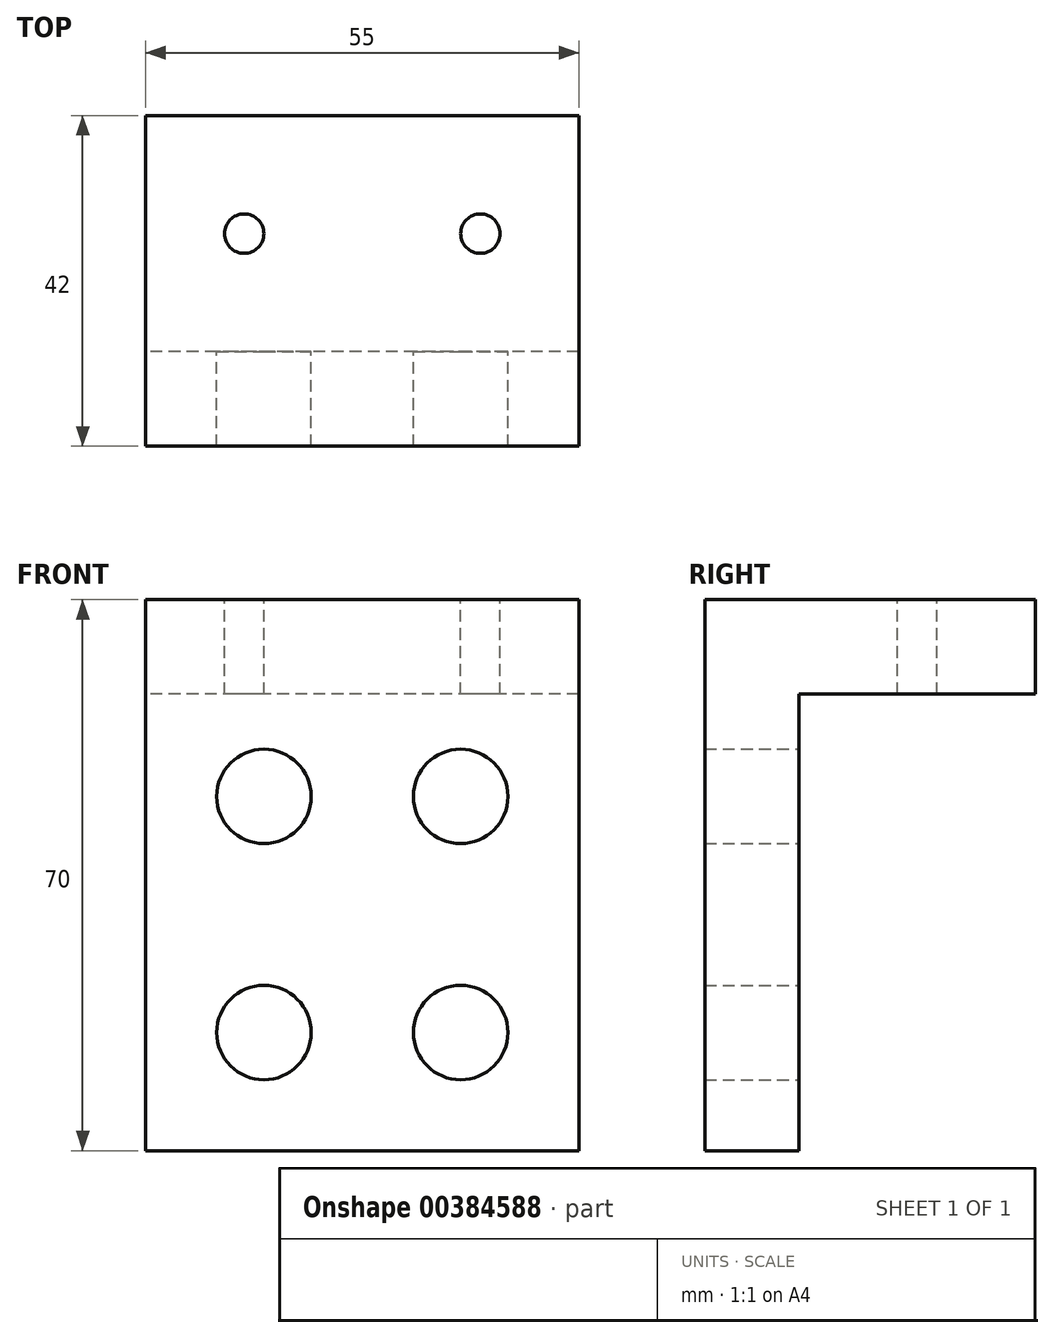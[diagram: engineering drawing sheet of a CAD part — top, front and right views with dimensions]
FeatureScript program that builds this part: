
annotation { "Feature Type Name" : "Feature", "Feature Type Description" : "" }
export const myFeature = defineFeature(function(context is Context, id is Id, definition is map)
    precondition{}
    {
        {
            var Q0;
            Q0=qCreatedBy(makeId("Top.planeOp"),FACE);
            var sketch = newSketch(context, id + "F0", { "sketchPlane" : qUnion([Q0])});
            skLineSegment(sketch, "E0.bottom", {"start": v(27.5, -15) * mm, "end": v(-27.5, -15) * mm});
            skLineSegment(sketch, "E0.top", {"start": v(27.5, 15) * mm, "end": v(-27.5, 15) * mm});
            skLineSegment(sketch, "E0.left", {"start": v(27.5, -15) * mm, "end": v(27.5, 15) * mm});
            skLineSegment(sketch, "E0.right", {"start": v(-27.5, -15) * mm, "end": v(-27.5, 15) * mm});
            skPoint(sketch, "E0.middle", {"position": v(0, 0) * mm});
            skSolve(sketch);
        }
        {
            var Q0;
            Q0=makeQuery(id+"F0.imprint","IMPRINT",FACE,{"disambiguationData":[TD([[makeQuery(id+"F0.imprint","IMPRINT",EDGE,{"derivedFrom":sQuery(id+"F0.wireOp",EDGE,"E0.bottom")}),-1.0]])]});
            extrude(context, id + "F1", {"entities" : qUnion([Q0]), "depth" : 12 * mm});
        }
        {
            var Q0;
            Q0=makeQuery(id+"F1.opExtrude","CAP_FACE",FACE,{"disambiguationData":[OSD([sQuery(id+"F0.wireOp",EDGE,"E0.bottom"),sQuery(id+"F0.wireOp",EDGE,"E0.top"),sQuery(id+"F0.wireOp",EDGE,"E0.left"),sQuery(id+"F0.wireOp",EDGE,"E0.right")])],"isStart":false});
            var sketch = newSketch(context, id + "F2", { "sketchPlane" : qUnion([Q0])});
            skLineSegment(sketch, "E1", {"start": v(-27.5, 0) * mm, "end": v(-15, 0) * mm, "construction": true});
            skLineSegment(sketch, "E2", {"start": v(-15, 0) * mm, "end": v(15, 0) * mm, "construction": true});
            skLineSegment(sketch, "E3", {"start": v(15, 0) * mm, "end": v(27.5, 0) * mm, "construction": true});
            skSolve(sketch);
        }
        {
            var Q0;
            Q0=sQuery(id+"F2.wireOp",VERTEX,"E2.start");
            var Q1;
            Q1=sQuery(id+"F2.wireOp",VERTEX,"E3.start");
            var Q2;
            Q2=makeQuery(id+"F1.opExtrude","SWEPT_BODY",BODY,{"disambiguationData":[OSD([sQuery(id+"F0.wireOp",EDGE,"E0.bottom"),sQuery(id+"F0.wireOp",EDGE,"E0.top"),sQuery(id+"F0.wireOp",EDGE,"E0.left"),sQuery(id+"F0.wireOp",EDGE,"E0.right")])]});
            hole(context, id + "F3", {"style" : HoleStyle.SIMPLE, "endStyle" : HoleEndStyle.BLIND, "holeDiameter" : 5 * mm, "holeDepth" : 25 * mm, "isTappedThrough" : true, "tappedDepth" : 12 * mm, "tapClearance" : 3, "locations" : qUnion([Q0, Q1]), "scope" : qUnion([Q2])});
        }
        {
            var Q0;
            Q0=makeQuery(id+"F1.opExtrude","SWEPT_FACE",FACE,{"disambiguationData":[OSD([sQuery(id+"F0.wireOp",EDGE,"E0.bottom")])]});
            var sketch = newSketch(context, id + "F4", { "sketchPlane" : qUnion([Q0])});
            skLineSegment(sketch, "E4.bottom", {"start": v(-27.5, 12) * mm, "end": v(27.5, 12) * mm});
            skLineSegment(sketch, "E4.top", {"start": v(-27.5, -58) * mm, "end": v(27.5, -58) * mm});
            skLineSegment(sketch, "E4.left", {"start": v(-27.5, 12) * mm, "end": v(-27.5, -58) * mm});
            skLineSegment(sketch, "E4.right", {"start": v(27.5, 12) * mm, "end": v(27.5, -58) * mm});
            skSolve(sketch);
        }
        {
            var Q0;
            {var subQ0=sQuery(id+"F4.wireOp",EDGE,"E4.top");Q0=makeQuery(id+"F4.imprint","IMPRINT",FACE,{"disambiguationData":[TD([[makeQuery(id+"F4.imprint","IMPRINT",EDGE,{"derivedFrom":subQ0}),1.0]])]});}
            var Q1;
            {var subQ0=sQuery(id+"F4.wireOp",EDGE,"E4.bottom");Q1=makeQuery(id+"F4.imprint","IMPRINT",FACE,{"disambiguationData":[TD([[makeQuery(id+"F4.imprint","IMPRINT",EDGE,{"derivedFrom":subQ0}),1.0]])]});}
            extrude(context, id + "F5", {"entities" : qUnion([Q0, Q1]), "operationType" : NewBodyOperationType.ADD, "depth" : 12 * mm});
        }
        {
            var Q0;
            Q0=makeQuery(id+"F5.opExtrude","CAP_FACE",FACE,{"disambiguationData":[OSD([sQuery(id+"F4.wireOp",EDGE,"E4.bottom"),sQuery(id+"F4.wireOp",EDGE,"E4.top"),sQuery(id+"F4.wireOp",EDGE,"E4.left"),sQuery(id+"F4.wireOp",EDGE,"E4.right")])],"isStart":true});
            var sketch = newSketch(context, id + "F6", { "sketchPlane" : qUnion([Q0])});
            skLineSegment(sketch, "E5", {"start": v(-27.5, -58) * mm, "end": v(-12.5, -58) * mm, "construction": true});
            skLineSegment(sketch, "E6", {"start": v(-12.5, -58) * mm, "end": v(-12.5, -43) * mm, "construction": true});
            skLineSegment(sketch, "E7", {"start": v(-12.5, -43) * mm, "end": v(-12.5, -13) * mm, "construction": true});
            skLineSegment(sketch, "E8", {"start": v(27.5, -58) * mm, "end": v(12.5, -58) * mm, "construction": true});
            skLineSegment(sketch, "E9", {"start": v(12.5, -58) * mm, "end": v(12.5, -43) * mm, "construction": true});
            skLineSegment(sketch, "E10", {"start": v(12.5, -43) * mm, "end": v(12.5, -13) * mm, "construction": true});
            skSolve(sketch);
        }
        {
            var Q0;
            Q0=sQuery(id+"F6.wireOp",VERTEX,"E10.end");
            var Q1;
            Q1=sQuery(id+"F6.wireOp",VERTEX,"E9.end");
            var Q2;
            Q2=sQuery(id+"F6.wireOp",VERTEX,"E7.start");
            var Q3;
            Q3=sQuery(id+"F6.wireOp",VERTEX,"E7.end");
            var Q4;
            Q4=makeQuery(id+"F1.opExtrude","SWEPT_BODY",BODY,{"disambiguationData":[OSD([sQuery(id+"F0.wireOp",EDGE,"E0.bottom"),sQuery(id+"F0.wireOp",EDGE,"E0.top"),sQuery(id+"F0.wireOp",EDGE,"E0.left"),sQuery(id+"F0.wireOp",EDGE,"E0.right")])]});
            hole(context, id + "F7", {"style" : HoleStyle.SIMPLE, "endStyle" : HoleEndStyle.BLIND, "holeDiameter" : 12 * mm, "holeDepth" : 12 * mm, "isTappedThrough" : true, "tappedDepth" : 12 * mm, "tapClearance" : 3, "locations" : qUnion([Q0, Q1, Q2, Q3]), "scope" : qUnion([Q4])});
        }
    });
